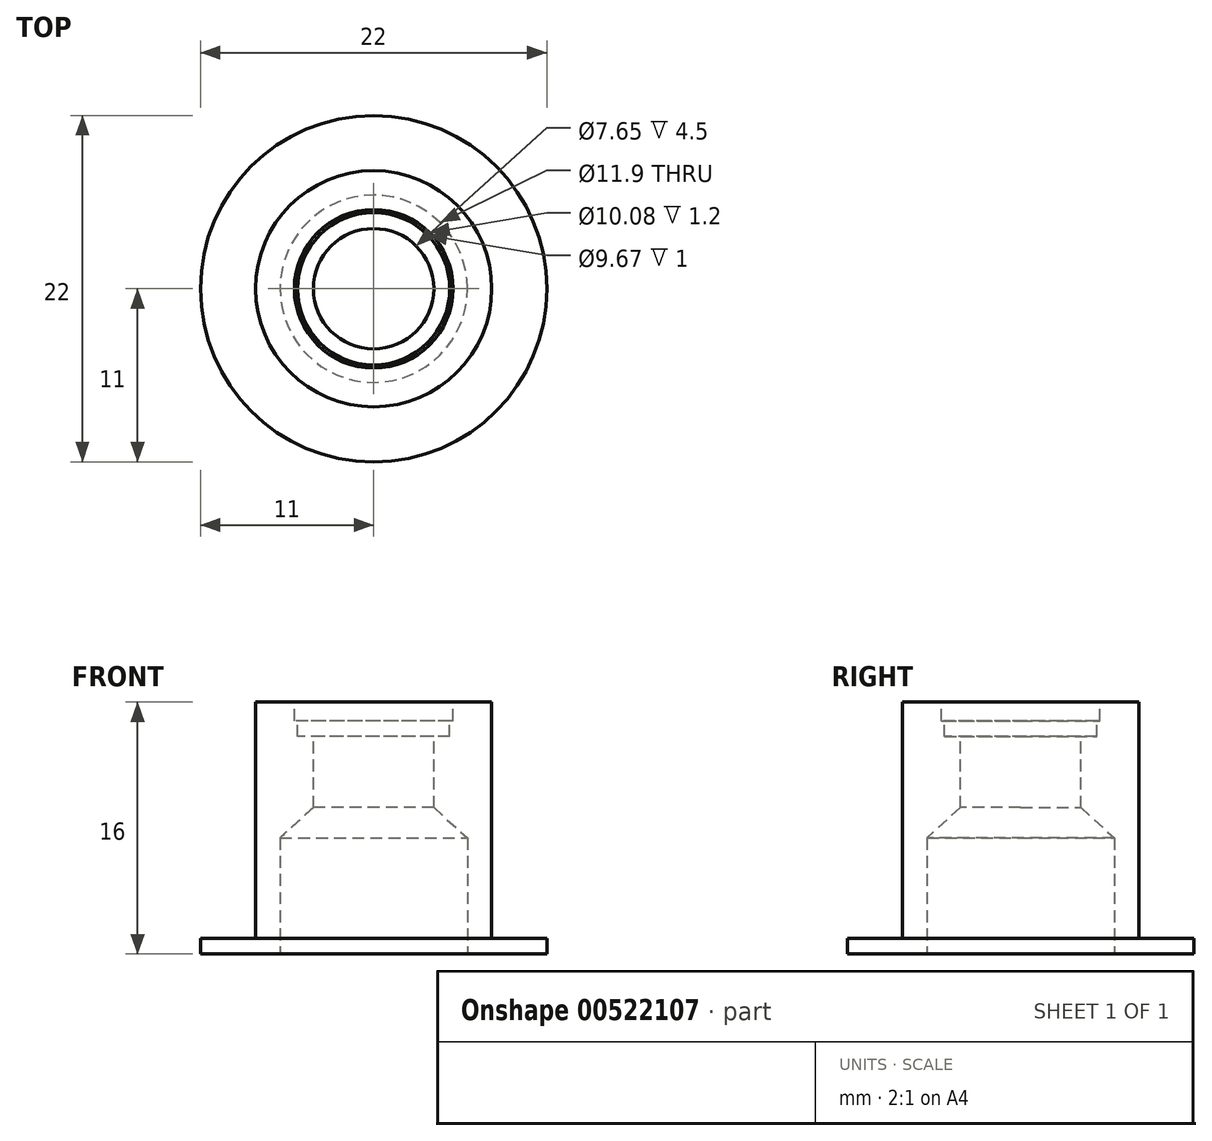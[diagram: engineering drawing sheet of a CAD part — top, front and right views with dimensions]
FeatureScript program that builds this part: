
annotation { "Feature Type Name" : "Feature", "Feature Type Description" : "" }
export const myFeature = defineFeature(function(context is Context, id is Id, definition is map)
    precondition{}
    {
        {
            var Q0;
            Q0=qCreatedBy(makeId("Top.planeOp"),FACE);
            var sketch = newSketch(context, id + "F0", { "sketchPlane" : qUnion([Q0])});
            skCircle(sketch, "E0", {"center": v(0, 0) * mm, "radius": 11 * mm});
            skSolve(sketch);
        }
        {
            var Q0;
            Q0 = qSketchRegion(id + "F0", true);
            extrude(context, id + "F1", {"entities" : qUnion([Q0]), "depth" : 1 * mm, "offsetDistance" : 25 * mm});
        }
        {
            var Q0;
            Q0=makeQuery(id+"F1.opExtrude","CAP_FACE",FACE,{"disambiguationData":[OSD([sQuery(id+"F0.wireOp",EDGE,"E0")])],"isStart":false});
            var sketch = newSketch(context, id + "F2", { "sketchPlane" : qUnion([Q0])});
            skCircle(sketch, "E1", {"center": v(0, 0) * mm, "radius": 7.5 * mm});
            skSolve(sketch);
        }
        {
            var Q0;
            Q0=makeQuery(id+"F2.imprint","IMPRINT",FACE,{"disambiguationData":[TD([[makeQuery(id+"F2.imprint","IMPRINT",EDGE,{"derivedFrom":sQuery(id+"F2.wireOp",EDGE,"E1")}),1.0]])]});
            extrude(context, id + "F3", {"entities" : qUnion([Q0]), "operationType" : NewBodyOperationType.ADD, "depth" : 15 * mm, "offsetDistance" : 25 * mm});
        }
        {
            var Q0;
            Q0=makeQuery(id+"F3.opExtrude","CAP_FACE",FACE,{"disambiguationData":[OSD([sQuery(id+"F2.wireOp",EDGE,"E1")])],"isStart":false});
            var sketch = newSketch(context, id + "F4", { "sketchPlane" : qUnion([Q0])});
            skCircle(sketch, "E2", {"center": v(0, 0) * mm, "radius": 3.83 * mm});
            skSolve(sketch);
        }
        {
            var Q0;
            Q0 = qSketchRegion(id + "F4", true);
            extrude(context, id + "F5", {"entities" : qUnion([Q0]), "operationType" : NewBodyOperationType.REMOVE, "oppositeDirection" : true, "depth" : 25 * mm, "offsetDistance" : 25 * mm});
        }
        {
            var Q0;
            Q0=makeQuery(id+"F1.opExtrude","CAP_FACE",FACE,{"disambiguationData":[OSD([sQuery(id+"F0.wireOp",EDGE,"E0")])],"isStart":true});
            var sketch = newSketch(context, id + "F6", { "sketchPlane" : qUnion([Q0])});
            skCircle(sketch, "E3", {"center": v(0, 0) * mm, "radius": 5.95 * mm});
            skSolve(sketch);
        }
        {
            var Q0;
            Q0 = qSketchRegion(id + "F6", true);
            extrude(context, id + "F7", {"entities" : qUnion([Q0]), "operationType" : NewBodyOperationType.REMOVE, "oppositeDirection" : true, "depth" : 7.3 * mm, "offsetDistance" : 25 * mm});
        }
        {
            var Q0;
            Q0=makeQuery(id+"F3.opExtrude","CAP_FACE",FACE,{"disambiguationData":[OSD([sQuery(id+"F2.wireOp",EDGE,"E1")])],"isStart":false});
            var sketch = newSketch(context, id + "F8", { "sketchPlane" : qUnion([Q0])});
            skCircle(sketch, "E4", {"center": v(0, 0) * mm, "radius": 5.04 * mm});
            skSolve(sketch);
        }
        {
            var Q0;
            Q0=makeQuery(id+"F8.imprint","IMPRINT",FACE,{"disambiguationData":[TD([[makeQuery(id+"F8.imprint","IMPRINT",EDGE,{"derivedFrom":sQuery(id+"F8.wireOp",EDGE,"E4")}),1.0]])]});
            extrude(context, id + "F9", {"entities" : qUnion([Q0]), "operationType" : NewBodyOperationType.REMOVE, "oppositeDirection" : true, "depth" : 1.2 * mm, "offsetDistance" : 25 * mm});
        }
        {
            var Q0;
            Q0=makeQuery(id+"F7.boolean.opBoolean","INTERSECT",EDGE,{"derivedFrom":[makeQuery(id+"F5.boolean.opBoolean","COPY",FACE,{"derivedFrom":makeQuery(id+"F5.opExtrude","SWEPT_FACE",FACE,{"disambiguationData":[OSD([sQuery(id+"F4.wireOp",EDGE,"E2")])]})}),makeQuery(id+"F7.opExtrude","CAP_FACE",FACE,{"disambiguationData":[OSD([sQuery(id+"F6.wireOp",EDGE,"E3")])],"isStart":false})]});
            chamfer(context, id + "F10", {"entities" : qUnion([Q0]), "chamferType" : ChamferType.TWO_OFFSETS, "width1" : 2.2 * mm, "oppositeDirection" : false, "width2" : 2 * mm, "tangentPropagation" : true});
        }
        {
            var Q0;
            Q0=makeQuery(id+"F9.boolean.opBoolean","COPY",FACE,{"derivedFrom":makeQuery(id+"F9.opExtrude","CAP_FACE",FACE,{"disambiguationData":[OSD([sQuery(id+"F4.wireOp",EDGE,"E2"),sQuery(id+"F8.wireOp",EDGE,"E4")])],"isStart":false})});
            var sketch = newSketch(context, id + "F11", { "sketchPlane" : qUnion([Q0])});
            skCircle(sketch, "E5.0", {"center": v(0, 0) * mm, "radius": 4.83 * mm});
            skSolve(sketch);
        }
        {
            var Q0;
            Q0=makeQuery(id+"F11.imprint","IMPRINT",FACE,{"disambiguationData":[TD([[makeQuery(id+"F11.imprint","IMPRINT",EDGE,{"derivedFrom":sQuery(id+"F11.wireOp",EDGE,"E5.0")}),1.0]])]});
            extrude(context, id + "F12", {"entities" : qUnion([Q0]), "operationType" : NewBodyOperationType.REMOVE, "oppositeDirection" : true, "depth" : 1 * mm, "offsetDistance" : 25 * mm});
        }
    });
